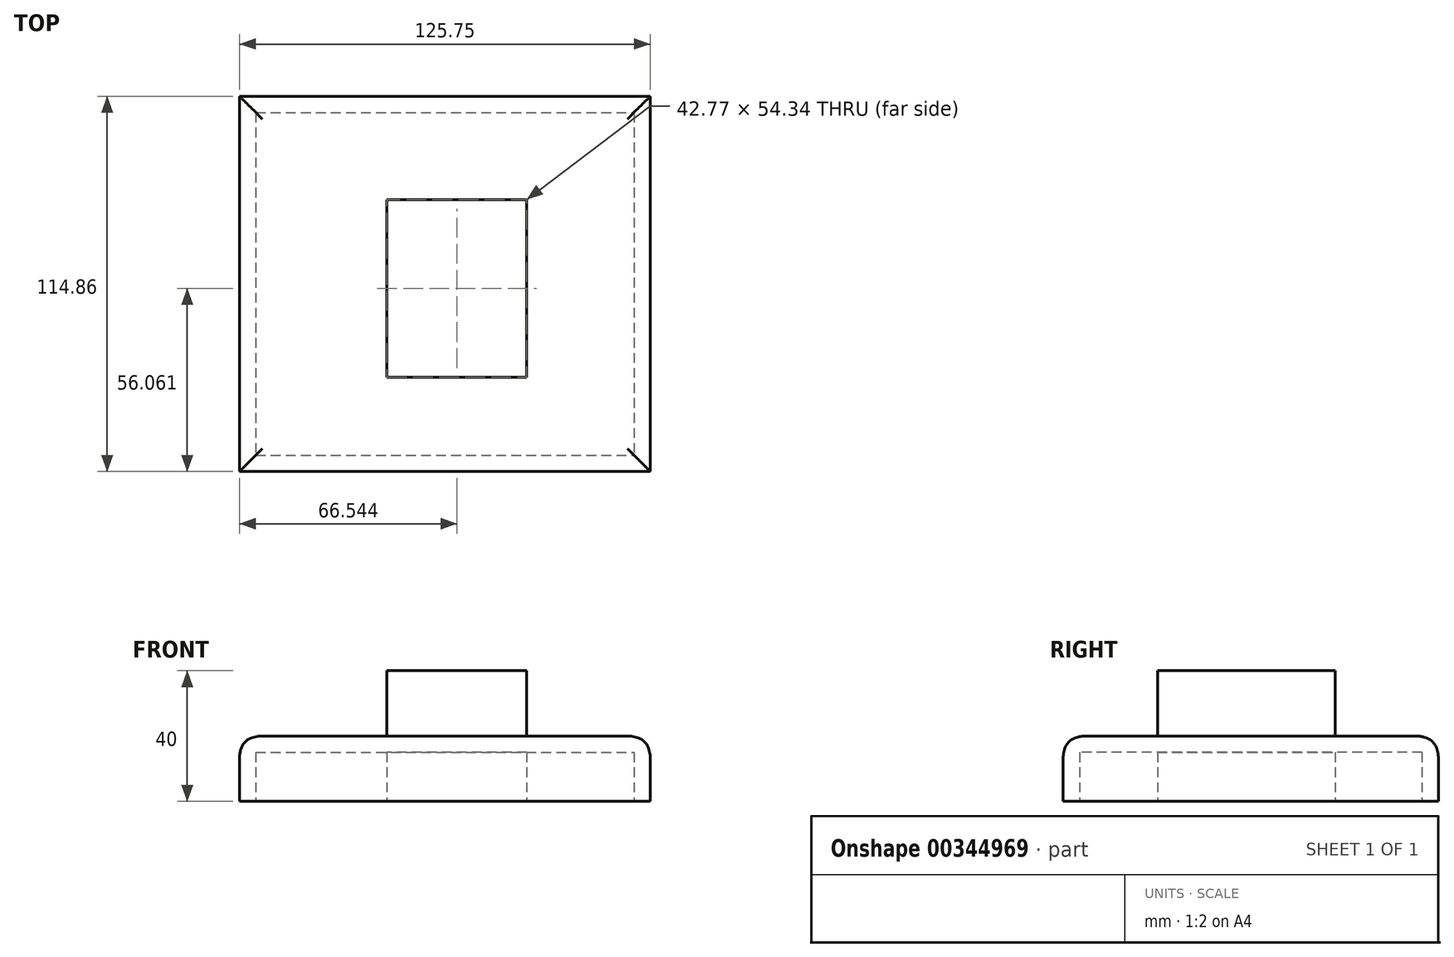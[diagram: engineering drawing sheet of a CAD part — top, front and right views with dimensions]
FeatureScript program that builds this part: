
annotation { "Feature Type Name" : "Feature", "Feature Type Description" : "" }
export const myFeature = defineFeature(function(context is Context, id is Id, definition is map)
    precondition{}
    {
        {
            var Q0;
            Q0=qCreatedBy(makeId("Top.planeOp"),FACE);
            var sketch = newSketch(context, id + "F0", { "sketchPlane" : qUnion([Q0])});
            skLineSegment(sketch, "E0.bottom", {"start": v(-65.05, 61.2) * mm, "end": v(60.7, 61.2) * mm});
            skLineSegment(sketch, "E0.top", {"start": v(-65.05, -53.66) * mm, "end": v(60.7, -53.66) * mm});
            skLineSegment(sketch, "E0.left", {"start": v(-65.05, 61.2) * mm, "end": v(-65.05, -53.66) * mm});
            skLineSegment(sketch, "E0.right", {"start": v(60.7, 61.2) * mm, "end": v(60.7, -53.66) * mm});
            skSolve(sketch);
        }
        {
            var Q0;
            Q0=makeQuery(id+"F0.imprint","IMPRINT",FACE,{"disambiguationData":[TD([[makeQuery(id+"F0.imprint","IMPRINT",EDGE,{"derivedFrom":sQuery(id+"F0.wireOp",EDGE,"E0.bottom")}),-1.0]])]});
            var sketch = newSketch(context, id + "F1", { "sketchPlane" : qUnion([Q0])});
            skSolve(sketch);
        }
        {
            var Q0;
            Q0=makeQuery(id+"F1.imprint","IMPRINT",FACE,{"disambiguationData":[TD([[makeQuery(id+"F1.imprint","IMPRINT",EDGE,{"derivedFrom":makeQuery(id+"F0.imprint","IMPRINT",EDGE,{"derivedFrom":sQuery(id+"F0.wireOp",EDGE,"E0.bottom")})}),-1.0]])]});
            extrude(context, id + "F2", {"entities" : qUnion([Q0]), "depth" : 20 * mm});
        }
        {
            var Q0;
            Q0=makeQuery(id+"F2.opExtrude","CAP_FACE",FACE,{"disambiguationData":[OSD([sQuery(id+"F0.wireOp",EDGE,"E0.bottom"),sQuery(id+"F0.wireOp",EDGE,"E0.top"),sQuery(id+"F0.wireOp",EDGE,"E0.left"),sQuery(id+"F0.wireOp",EDGE,"E0.right")])],"isStart":true});
            shell(context, id + "F3", {"entities" : qUnion([Q0]), "thickness" : 5 * mm});
        }
        {
            var Q0;
            Q0=makeQuery(id+"F2.opExtrude","CAP_FACE",FACE,{"disambiguationData":[OSD([sQuery(id+"F0.wireOp",EDGE,"E0.bottom"),sQuery(id+"F0.wireOp",EDGE,"E0.top"),sQuery(id+"F0.wireOp",EDGE,"E0.left"),sQuery(id+"F0.wireOp",EDGE,"E0.right")])],"isStart":false});
            var sketch = newSketch(context, id + "F4", { "sketchPlane" : qUnion([Q0])});
            skCircle(sketch, "E1", {"center": v(-27.02, -33.12) * mm, "radius": 10.4 * mm});
            skSolve(sketch);
        }
        {
            var Q0;
            Q0=qCreatedBy(makeId("Top.planeOp"),FACE);
            var sketch = newSketch(context, id + "F5", { "sketchPlane" : qUnion([Q0])});
            skLineSegment(sketch, "E2.bottom", {"start": v(-19.89, 29.57) * mm, "end": v(22.88, 29.57) * mm});
            skLineSegment(sketch, "E2.top", {"start": v(-19.89, -24.77) * mm, "end": v(22.88, -24.77) * mm});
            skLineSegment(sketch, "E2.left", {"start": v(-19.89, 29.57) * mm, "end": v(-19.89, -24.77) * mm});
            skLineSegment(sketch, "E2.right", {"start": v(22.88, 29.57) * mm, "end": v(22.88, -24.77) * mm});
            skLineSegment(sketch, "E3.bottom", {"start": v(22.88, -24.77) * mm, "end": v(-19.89, -24.77) * mm});
            skLineSegment(sketch, "E3.top", {"start": v(22.88, 29.57) * mm, "end": v(-19.89, 29.57) * mm});
            skLineSegment(sketch, "E3.left", {"start": v(22.88, -24.77) * mm, "end": v(22.88, 29.57) * mm});
            skLineSegment(sketch, "E3.right", {"start": v(-19.89, -24.77) * mm, "end": v(-19.89, 29.57) * mm});
            skSolve(sketch);
        }
        {
            var Q0;
            Q0 = qSketchRegion(id + "F5", true);
            extrude(context, id + "F6", {"entities" : qUnion([Q0]), "operationType" : NewBodyOperationType.ADD, "depth" : 40 * mm});
        }
        {
            var Q0;
            Q0=makeQuery(id+"F2.opExtrude","CAP_EDGE",EDGE,{"disambiguationData":[OSD([sQuery(id+"F0.wireOp",EDGE,"E0.left")])],"isStart":false});
            var Q1;
            Q1=makeQuery(id+"F2.opExtrude","CAP_EDGE",EDGE,{"disambiguationData":[OSD([sQuery(id+"F0.wireOp",EDGE,"E0.top")])],"isStart":false});
            var Q2;
            Q2=makeQuery(id+"F2.opExtrude","CAP_EDGE",EDGE,{"disambiguationData":[OSD([sQuery(id+"F0.wireOp",EDGE,"E0.right")])],"isStart":false});
            var Q3;
            Q3=makeQuery(id+"F2.opExtrude","CAP_EDGE",EDGE,{"disambiguationData":[OSD([sQuery(id+"F0.wireOp",EDGE,"E0.bottom")])],"isStart":false});
            fillet(context, id + "F7", {"entities" : qUnion([Q0, Q1, Q2, Q3]), "radius" : 7 * mm, "tangentPropagation" : true, "rho" : 0.5, "crossSection" : FilletCrossSection.CONIC, "allowEdgeOverflow" : false});
        }
    });
